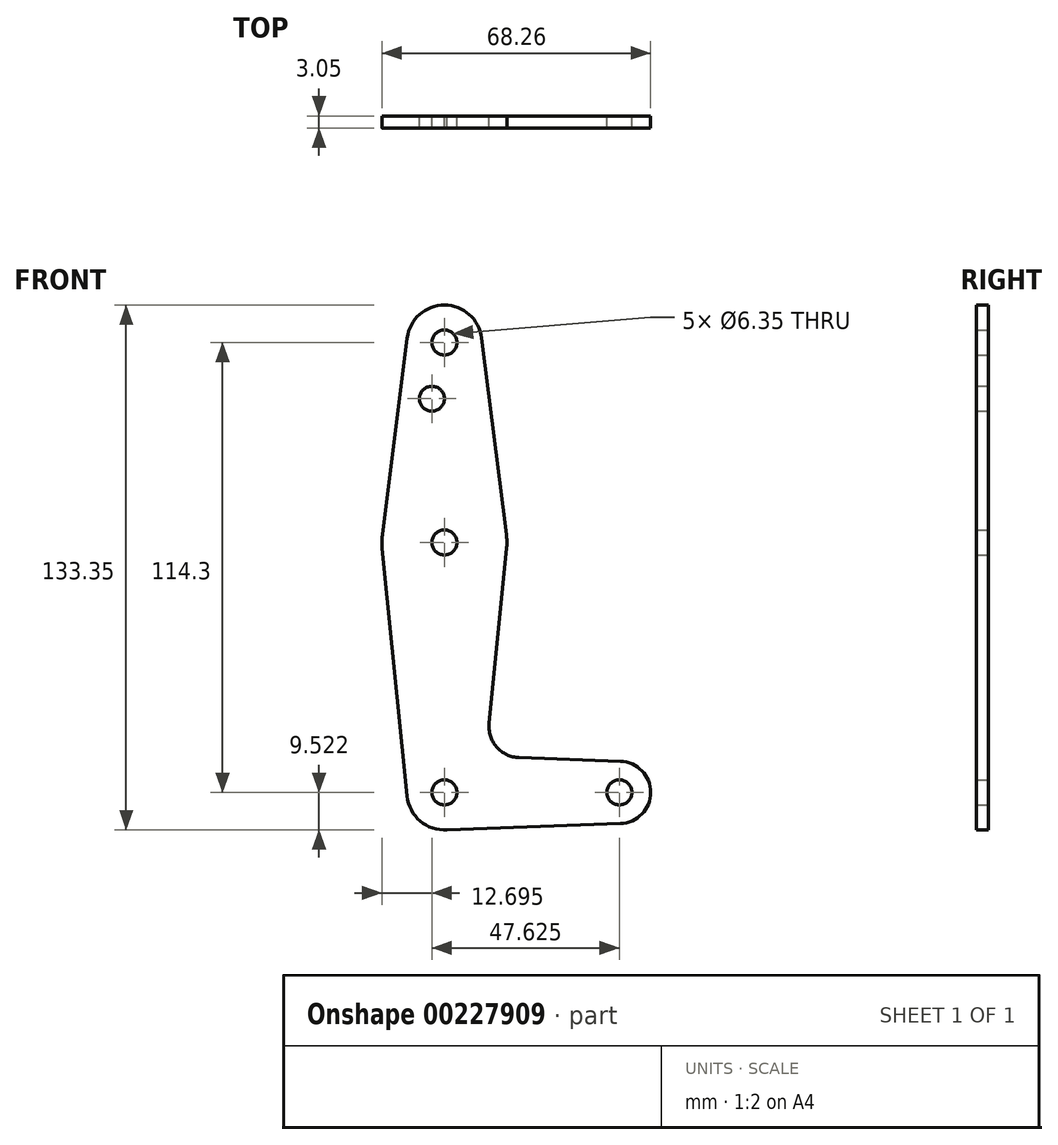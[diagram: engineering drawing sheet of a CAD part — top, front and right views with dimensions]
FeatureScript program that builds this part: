
annotation { "Feature Type Name" : "Feature", "Feature Type Description" : "" }
export const myFeature = defineFeature(function(context is Context, id is Id, definition is map)
    precondition{}
    {
        {
            var Q0;
            Q0=qCreatedBy(makeId("Front.planeOp"),FACE);
            var sketch = newSketch(context, id + "F0", { "sketchPlane" : qUnion([Q0])});
            skCircle(sketch, "E0", {"center": v(0, 64.48) * mm, "radius": 9.53 * mm});
            skCircle(sketch, "E1", {"center": v(0, 13.68) * mm, "radius": 15.88 * mm});
            skLineSegment(sketch, "E2", {"start": v(0, -49.82) * mm, "end": v(44.45, -49.82) * mm, "construction": true});
            skCircle(sketch, "E3", {"center": v(0, -49.82) * mm, "radius": 9.53 * mm});
            skCircle(sketch, "E4", {"center": v(44.45, -49.82) * mm, "radius": 7.94 * mm});
            skLineSegment(sketch, "E5", {"start": v(-9.45, 65.67) * mm, "end": v(-15.75, 15.67) * mm});
            skLineSegment(sketch, "E6", {"start": v(9.45, 65.67) * mm, "end": v(15.75, 15.67) * mm});
            skLineSegment(sketch, "E7", {"start": v(-15.8, 12.1) * mm, "end": v(-9.48, -50.77) * mm});
            skLineSegment(sketch, "E8", {"start": v(15.8, 12.1) * mm, "end": v(11.34, -32.23) * mm});
            skLineSegment(sketch, "E9", {"start": v(18.97, -40.97) * mm, "end": v(44.73, -41.89) * mm});
            skLineSegment(sketch, "E10", {"start": v(0, -59.34) * mm, "end": v(44.73, -57.75) * mm});
            skLineSegment(sketch, "E11", {"start": v(0, 64.48) * mm, "end": v(0, -49.82) * mm, "construction": true});
            skCircle(sketch, "E12", {"center": v(0, 64.48) * mm, "radius": 3.18 * mm});
            skCircle(sketch, "E13", {"center": v(0, 13.68) * mm, "radius": 3.18 * mm});
            skCircle(sketch, "E14", {"center": v(0, -49.82) * mm, "radius": 3.18 * mm});
            skCircle(sketch, "E15", {"center": v(44.45, -49.82) * mm, "radius": 3.18 * mm});
            skCircle(sketch, "E16", {"center": v(-3.18, 50.2) * mm, "radius": 3.18 * mm});
            skArc(sketch, "E17.filletArc", {"start": v(11.34, -32.23) * mm, "mid": v(13.26, -38.25) * mm, "end": v(18.97, -40.97) * mm});
            skSolve(sketch);
        }
        {
            var Q0;
            Q0 = qSketchRegion(id + "F0", true);
            extrude(context, id + "F1", {"entities" : qUnion([Q0]), "depth" : 3.05 * mm});
        }
    });
